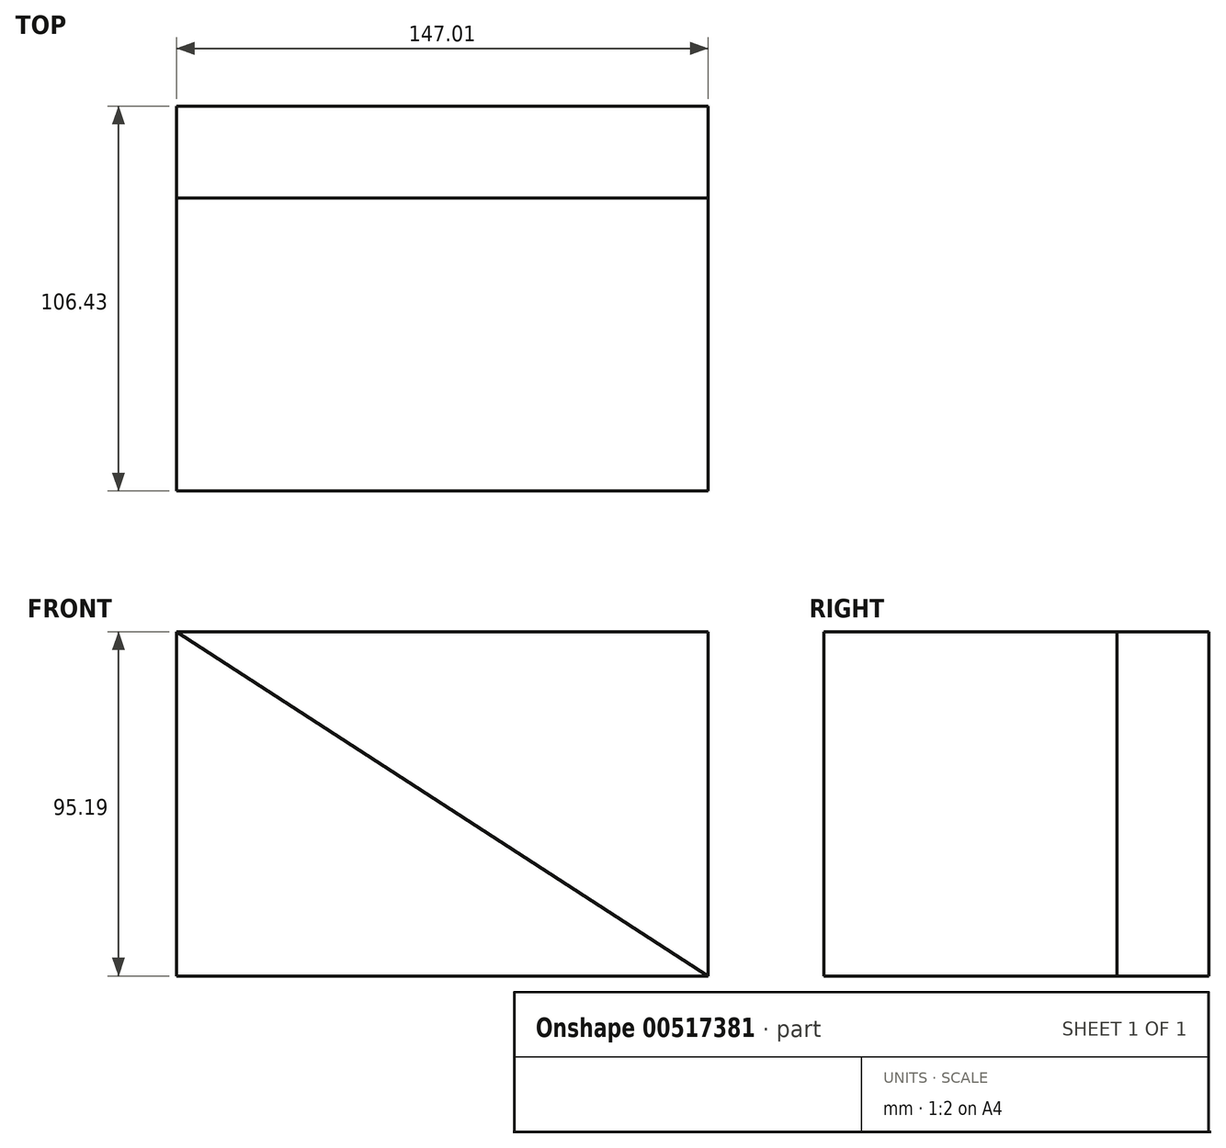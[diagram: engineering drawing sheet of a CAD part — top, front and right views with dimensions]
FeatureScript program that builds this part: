
annotation { "Feature Type Name" : "Feature", "Feature Type Description" : "" }
export const myFeature = defineFeature(function(context is Context, id is Id, definition is map)
    precondition{}
    {
        {
            var Q0;
            Q0=qCreatedBy(makeId("Front.planeOp"),FACE);
            var sketch = newSketch(context, id + "F0", { "sketchPlane" : qUnion([Q0])});
            skLineSegment(sketch, "E0.bottom", {"start": v(-71.58, 55.67) * mm, "end": v(75.43, 55.67) * mm});
            skLineSegment(sketch, "E0.top", {"start": v(-71.58, -39.52) * mm, "end": v(75.43, -39.52) * mm});
            skLineSegment(sketch, "E0.left", {"start": v(-71.58, 55.67) * mm, "end": v(-71.58, -39.52) * mm});
            skLineSegment(sketch, "E0.right", {"start": v(75.43, 55.67) * mm, "end": v(75.43, -39.52) * mm});
            skLineSegment(sketch, "E1", {"start": v(-71.58, 55.67) * mm, "end": v(75.43, -39.52) * mm});
            skSolve(sketch);
        }
        {
            var Q0;
            Q0=makeQuery(id+"F0.imprint","IMPRINT",FACE,{"disambiguationData":[TD([[makeQuery(id+"F0.imprint","IMPRINT",EDGE,{"derivedFrom":sQuery(id+"F0.wireOp",EDGE,"E0.top")}),1.0]])]});
            extrude(context, id + "F1", {"entities" : qUnion([Q0]), "depth" : 106.43 * mm, "offsetDistance" : 25.4 * mm});
        }
        {
            var Q0;
            Q0 = qSketchRegion(id + "F0", true);
            extrude(context, id + "F2", {"entities" : qUnion([Q0]), "operationType" : NewBodyOperationType.ADD, "depth" : 25.4 * mm, "offsetDistance" : 25.4 * mm});
        }
    });
